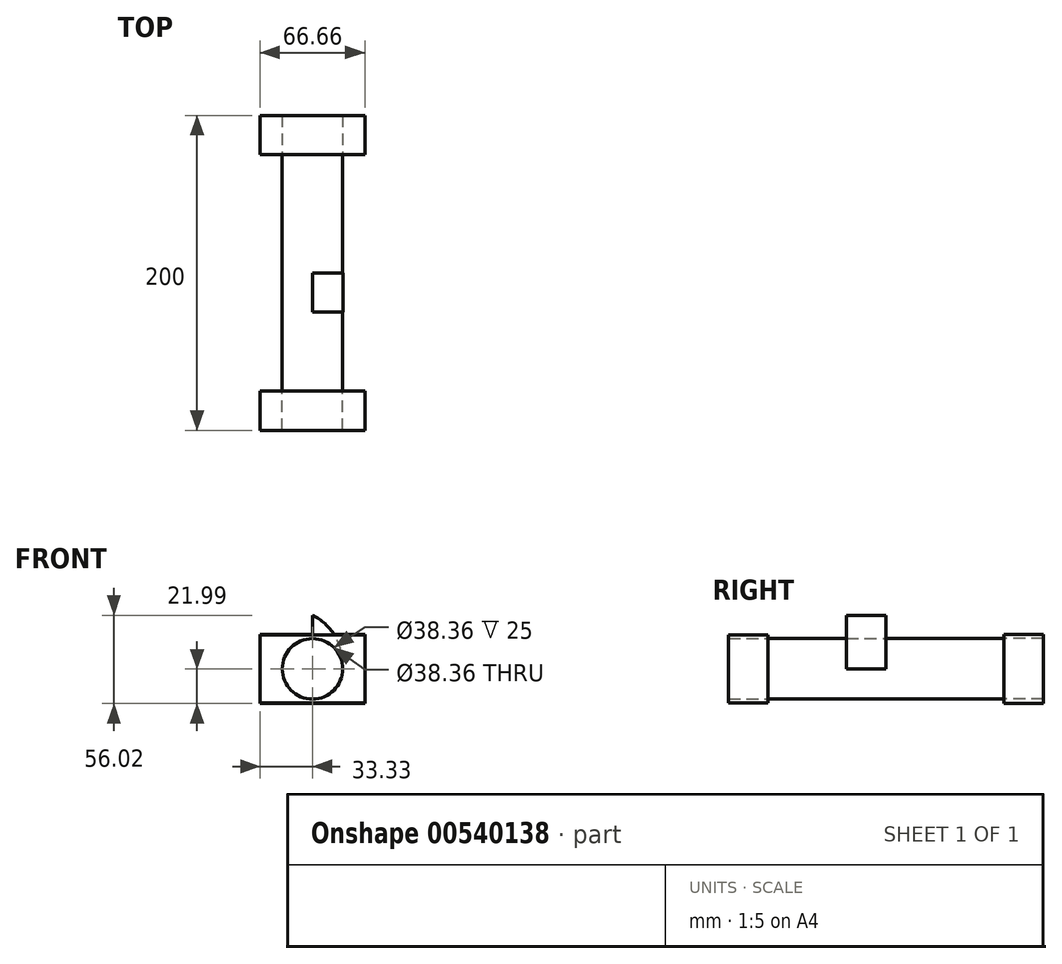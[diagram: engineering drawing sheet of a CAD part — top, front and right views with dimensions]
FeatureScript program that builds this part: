
annotation { "Feature Type Name" : "Feature", "Feature Type Description" : "" }
export const myFeature = defineFeature(function(context is Context, id is Id, definition is map)
    precondition{}
    {
        {
            var Q0;
            Q0=qCreatedBy(makeId("Front.planeOp"),FACE);
            var sketch = newSketch(context, id + "F0", { "sketchPlane" : qUnion([Q0])});
            skCircle(sketch, "E0", {"center": v(0, 0) * mm, "radius": 19.18 * mm});
            skLineSegment(sketch, "E1", {"start": v(0, 19.18) * mm, "end": v(0, 34.03) * mm});
            skArc(sketch, "E2", {"start": v(19.18, 0) * mm, "mid": v(14.85, 19.98) * mm, "end": v(0, 34.03) * mm});
            skSolve(sketch);
        }
        {
            var Q0;
            {var subQ0=sQuery(id+"F0.wireOp",EDGE,"E0");var subQ1=makeQuery(id+"F0.imprint","INTERSECT",VERTEX,{"derivedFrom":[subQ0,sQuery(id+"F0.wireOp",EDGE,"E1")]});Q0=makeQuery(id+"F0.imprint","IMPRINT",FACE,{"disambiguationData":[TD([[makeQuery(id+"F0.imprint","IMPRINT",EDGE,{"disambiguationData":[TD([[subQ1,1.0]])],"derivedFrom":subQ0}),1.0]])]});}
            extrude(context, id + "F1", {"entities" : qUnion([Q0]), "endBound" : BoundingType.SYMMETRIC, "depth" : 150 * mm, "offsetDistance" : 25 * mm});
        }
        {
            var Q0;
            Q0 = qSketchRegion(id + "F0", true);
            extrude(context, id + "F2", {"entities" : qUnion([Q0]), "operationType" : NewBodyOperationType.ADD, "depth" : 25 * mm, "offsetDistance" : 25 * mm});
        }
        {
            var Q0;
            Q0=makeQuery(id+"F1.opExtrude","CAP_FACE",FACE,{"disambiguationData":[OSD([sQuery(id+"F0.wireOp",EDGE,"E0")])],"isStart":false});
            var sketch = newSketch(context, id + "F3", { "sketchPlane" : qUnion([Q0])});
            skLineSegment(sketch, "E3.bottom", {"start": v(-33.26, 21.47) * mm, "end": v(33.26, 21.47) * mm});
            skLineSegment(sketch, "E3.top", {"start": v(-33.26, -21.47) * mm, "end": v(33.26, -21.47) * mm});
            skLineSegment(sketch, "E3.left", {"start": v(-33.26, 21.47) * mm, "end": v(-33.26, -21.47) * mm});
            skLineSegment(sketch, "E3.right", {"start": v(33.26, 21.47) * mm, "end": v(33.26, -21.47) * mm});
            skPoint(sketch, "E3.middle", {"position": v(0, 0) * mm});
            skSolve(sketch);
        }
        {
            var Q0;
            Q0=makeQuery(id+"F3.imprint","IMPRINT",FACE,{"disambiguationData":[TD([[makeQuery(id+"F3.imprint","IMPRINT",EDGE,{"derivedFrom":sQuery(id+"F3.wireOp",EDGE,"E3.bottom")}),-1.0]])]});
            extrude(context, id + "F4", {"entities" : qUnion([Q0]), "depth" : 25 * mm, "offsetDistance" : 25 * mm});
        }
        {
            var Q0;
            Q0=makeQuery(id+"F1.opExtrude","CAP_FACE",FACE,{"disambiguationData":[OSD([sQuery(id+"F0.wireOp",EDGE,"E0")])],"isStart":true});
            var sketch = newSketch(context, id + "F5", { "sketchPlane" : qUnion([Q0])});
            skLineSegment(sketch, "E4.bottom", {"start": v(-33.33, 22) * mm, "end": v(33.33, 22) * mm});
            skLineSegment(sketch, "E4.top", {"start": v(-33.33, -22) * mm, "end": v(33.33, -22) * mm});
            skLineSegment(sketch, "E4.left", {"start": v(-33.33, 22) * mm, "end": v(-33.33, -22) * mm});
            skLineSegment(sketch, "E4.right", {"start": v(33.33, 22) * mm, "end": v(33.33, -22) * mm});
            skPoint(sketch, "E4.middle", {"position": v(0, 0) * mm});
            skSolve(sketch);
        }
        {
            var Q0;
            Q0=makeQuery(id+"F5.imprint","IMPRINT",FACE,{"disambiguationData":[TD([[makeQuery(id+"F5.imprint","IMPRINT",EDGE,{"derivedFrom":sQuery(id+"F5.wireOp",EDGE,"E4.bottom")}),-1.0]])]});
            extrude(context, id + "F6", {"entities" : qUnion([Q0]), "depth" : 25 * mm, "offsetDistance" : 25 * mm});
        }
    });
